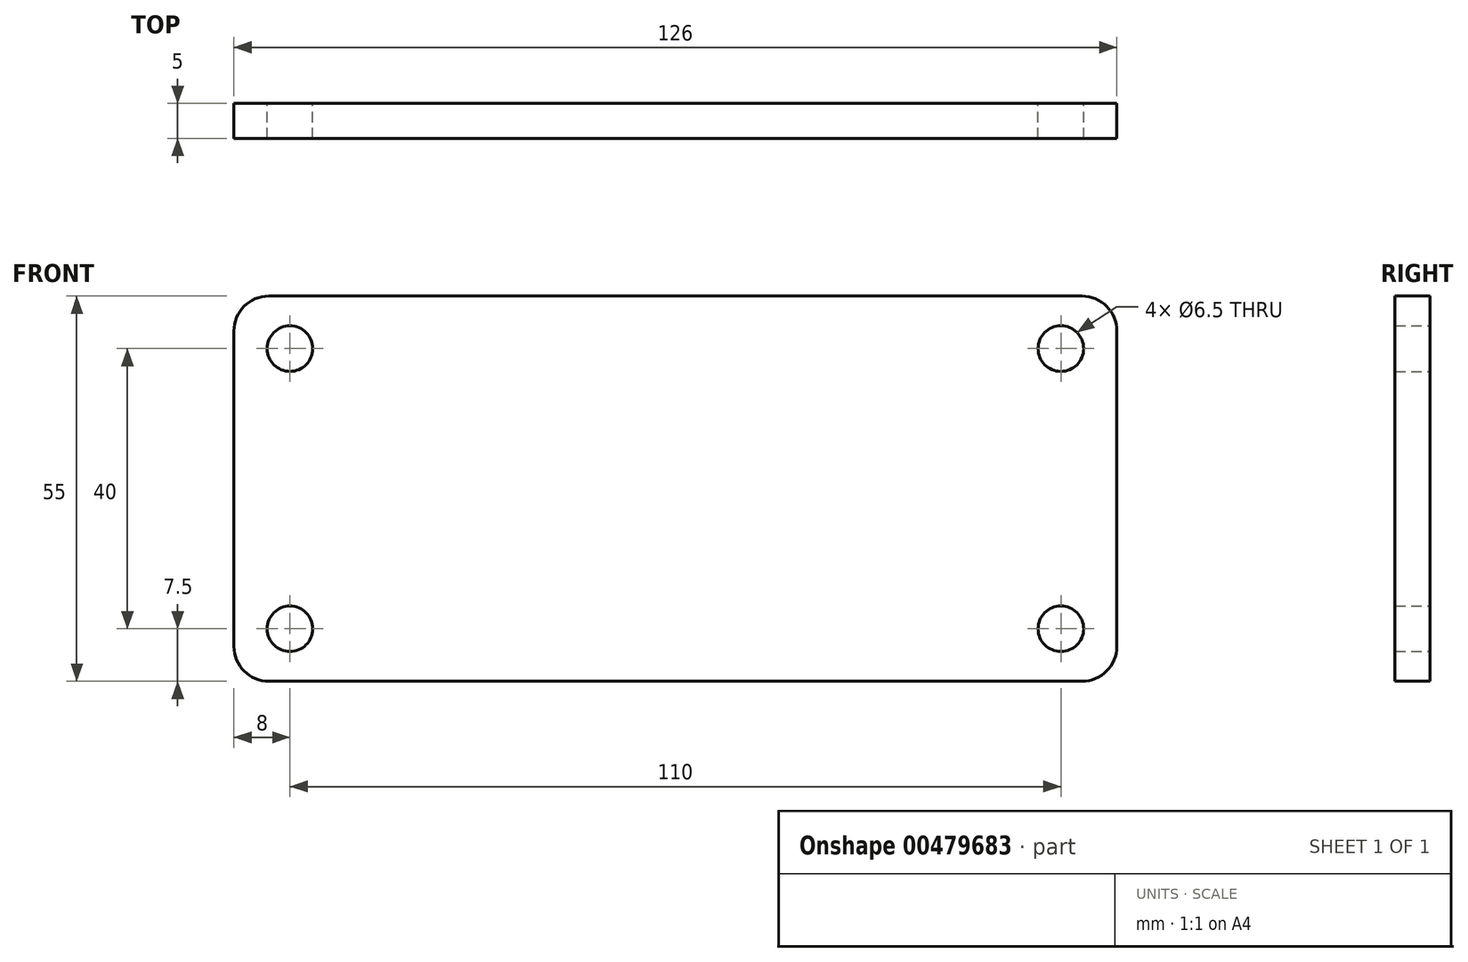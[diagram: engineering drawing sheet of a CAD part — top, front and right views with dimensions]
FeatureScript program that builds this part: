
annotation { "Feature Type Name" : "Feature", "Feature Type Description" : "" }
export const myFeature = defineFeature(function(context is Context, id is Id, definition is map)
    precondition{}
    {
        {
            var Q0;
            Q0=qCreatedBy(makeId("Front.planeOp"),FACE);
            var sketch = newSketch(context, id + "F0", { "sketchPlane" : qUnion([Q0])});
            skLineSegment(sketch, "E0.bottom", {"start": v(63, -27.5) * mm, "end": v(-63, -27.5) * mm});
            skLineSegment(sketch, "E0.top", {"start": v(63, 27.5) * mm, "end": v(-63, 27.5) * mm});
            skLineSegment(sketch, "E0.left", {"start": v(63, -27.5) * mm, "end": v(63, 27.5) * mm});
            skLineSegment(sketch, "E0.right", {"start": v(-63, -27.5) * mm, "end": v(-63, 27.5) * mm});
            skPoint(sketch, "E0.middle", {"position": v(0, 0) * mm});
            skCircle(sketch, "E1", {"center": v(-55, 20) * mm, "radius": 3.25 * mm});
            skCircle(sketch, "E2", {"center": v(-55, -20) * mm, "radius": 3.25 * mm});
            skCircle(sketch, "E3", {"center": v(55, 20) * mm, "radius": 3.25 * mm});
            skCircle(sketch, "E4", {"center": v(55, -20) * mm, "radius": 3.25 * mm});
            skSolve(sketch);
        }
        {
            var Q0;
            Q0=makeQuery(id+"F0.imprint","IMPRINT",FACE,{"disambiguationData":[TD([[makeQuery(id+"F0.imprint","IMPRINT",EDGE,{"derivedFrom":sQuery(id+"F0.wireOp",EDGE,"E0.bottom")}),-1.0]])]});
            extrude(context, id + "F1", {"entities" : qUnion([Q0]), "depth" : 5 * mm});
        }
        {
            var Q0;
            Q0=makeQuery(id+"F1.opExtrude","SWEPT_EDGE",EDGE,{"disambiguationData":[OSD([sQuery(id+"F0.wireOp",EDGE,"E0.top"),sQuery(id+"F0.wireOp",EDGE,"E0.left")])]});
            var Q1;
            Q1=makeQuery(id+"F1.opExtrude","SWEPT_EDGE",EDGE,{"disambiguationData":[OSD([sQuery(id+"F0.wireOp",EDGE,"E0.bottom"),sQuery(id+"F0.wireOp",EDGE,"E0.left")])]});
            var Q2;
            Q2=makeQuery(id+"F1.opExtrude","SWEPT_EDGE",EDGE,{"disambiguationData":[OSD([sQuery(id+"F0.wireOp",EDGE,"E0.top"),sQuery(id+"F0.wireOp",EDGE,"E0.right")])]});
            var Q3;
            Q3=makeQuery(id+"F1.opExtrude","SWEPT_EDGE",EDGE,{"disambiguationData":[OSD([sQuery(id+"F0.wireOp",EDGE,"E0.bottom"),sQuery(id+"F0.wireOp",EDGE,"E0.right")])]});
            fillet(context, id + "F2", {"entities" : qUnion([Q0, Q1, Q2, Q3]), "radius" : 5 * mm, "tangentPropagation" : true, "allowEdgeOverflow" : false});
        }
    });
